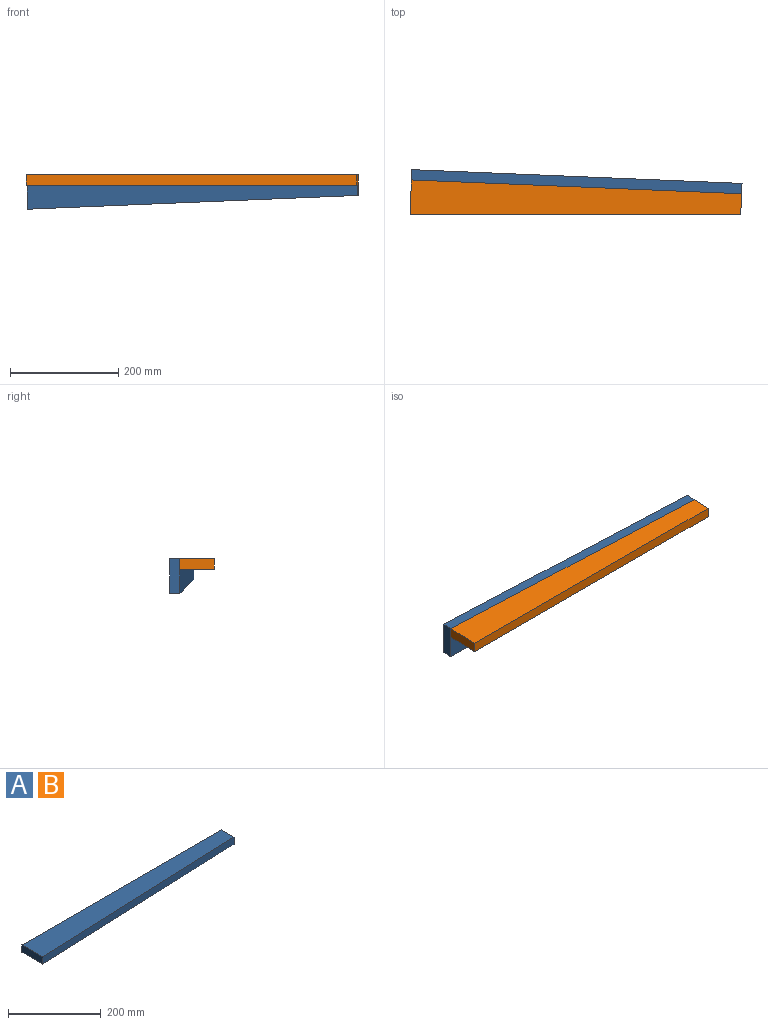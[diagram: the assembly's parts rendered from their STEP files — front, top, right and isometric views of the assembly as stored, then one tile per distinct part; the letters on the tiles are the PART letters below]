
ASSEMBLY  parts=2 mates=1
PART A: 6 faces, bbox 609.6x63.5x19.1 mm
  f0: plane 609.6x19.05mm, normal (0,1,0), area 11612.9mm2, adj f1,f3,f4,f5
  f1: plane 63.5x19.05mm, normal (-1,0,0), area 1209.7mm2, adj f0,f2,f4,f5
  f2: plane 609.6x25.4mm, normal (0.04,-1,0), area 11623mm2, adj f1,f3,f4,f5
  f3: plane 38.1x19.05mm, normal (1,0,0), area 725.8mm2, adj f0,f2,f4,f5
  f4: plane 609.6x63.5mm, normal (0,0,1), area 30967.7mm2, adj f0,f1,f2,f3
  f5: plane 609.6x63.5mm, normal (0,0,-1), area 30967.7mm2, adj f0,f1,f2,f3
PART B: same geometry as A
PLACE A rot(axis=(1,-0.02,-0.02),90deg) t=(-88.34,157.54,-119.55)mm
PLACE B rot(axis=(0,0,-1),2.4deg) t=(-91.78,75.06,-75.1)mm fixed
MATE fastened B.f1 <-> A.f1  axis (-1,0.04,0) through (-89.13,138.5,-56.05)mm
